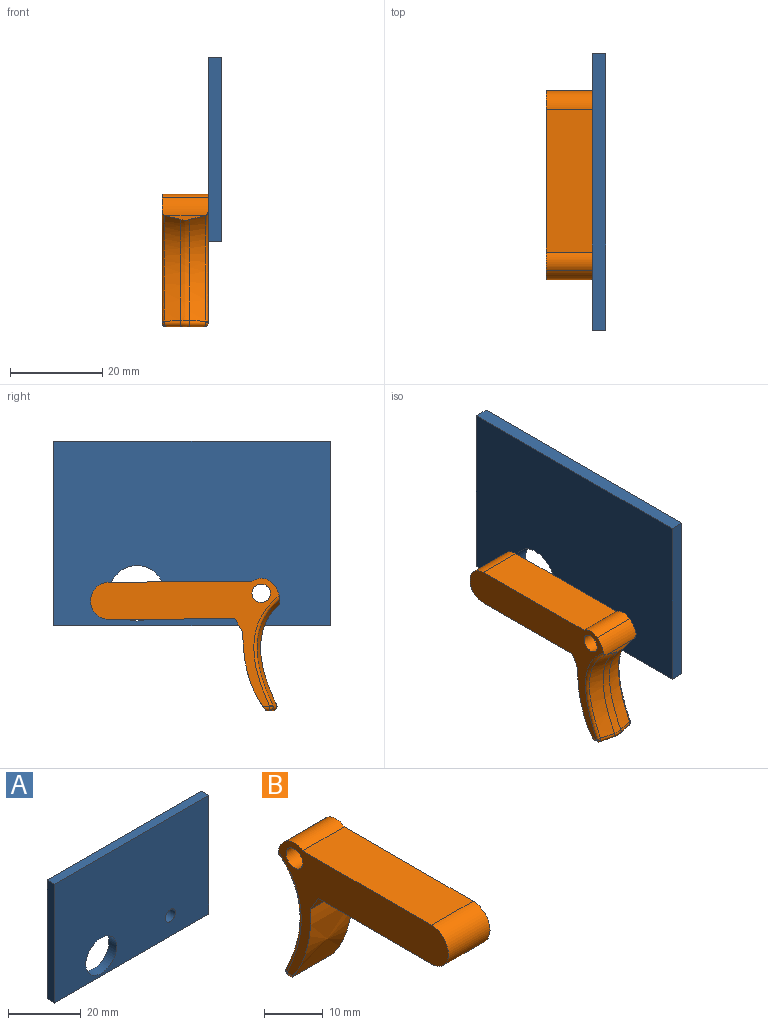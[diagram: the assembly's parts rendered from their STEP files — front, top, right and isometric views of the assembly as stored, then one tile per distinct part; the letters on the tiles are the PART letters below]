
ASSEMBLY  parts=2 mates=1
PART A: 8 faces, bbox 60x3x40 mm
  f0: plane 60x3mm, normal (0,0,-1), area 180mm2, adj f1,f5,f6,f7
  f1: plane 40x3mm, normal (1,0,0), area 120mm2, adj f0,f2,f6,f7
  f2: plane 60x3mm, normal (0,0,1), area 180mm2, adj f1,f5,f6,f7
  f3: cylinder r=2mm len=4mm, axis (0,1,0), area 37.7mm2, adj f6,f7
  f4: cylinder r=6mm len=12mm, axis (0,1,0), area 113.1mm2, adj f6,f7
  f5: plane 40x3mm, normal (-1,0,0), area 120mm2, adj f0,f2,f6,f7
  f6: plane 60x40mm, normal (0,-1,0), area 2274.3mm2, adj f0,f1,f2,f3,f4,f5
  f7: plane 60x40mm, normal (0,1,0), area 2274.3mm2, adj f0,f1,f2,f3,f4,f5
PART B: 27 faces, bbox 10.4x43.6x30.6 mm
  f0: cylinder r=4.04mm len=10mm, axis (-1,0,0), area 127mm2, adj f1,f7,f9,f10
  f1: plane 27.18x10mm, normal (0,0,-1), area 271.8mm2, adj f0,f2,f9,f10
  f2: plane 10x3.03mm, normal (0,-0.87,-0.5), area 35mm2, adj f1,f3,f9,f10
  f3: extruded ~16.65x10mm, area 176.3mm2, adj f2,f9,f10,f22,f24,f25
  f4: plane 8.2x0.99mm, normal (0,0,-1), area 5.1mm2, adj f16,f18,f21,f22,f24,f25
  f5: plane 8.11x1.11mm, normal (0,1,0), area 4.1mm2, adj f11,f12,f15,f26
  f6: cylinder r=3.25mm len=10mm, axis (-1,0,0), area 43.1mm2, adj f7,f9,f10,f26
  f7: plane 30.93x10mm, normal (0,0,1), area 309.3mm2, adj f0,f6,f9,f10
  f8: cylinder r=2mm len=10mm, axis (-1,0,0), area 125.7mm2, adj f9,f10
  f9: plane 40.89x28.4mm, normal (1,0,0), area 343.7mm2, adj f0,f1,f2,f3,f6,f7,f8,f14
  f10: plane 40.89x28.4mm, normal (-1,0,0), area 343.7mm2, adj f0,f1,f2,f3,f6,f7,f8,f13
  f11: bspline ~26.91x6.81mm, area 86mm2, adj f5,f13,f15,f16,f26
  f12: bspline ~26.91x6.81mm, area 86mm2, adj f5,f14,f15,f21,f26
  f13: bspline ~27.3x8.05mm, area 24.6mm2, adj f10,f11,f17,f26
  f14: bspline ~27.35x8.1mm, area 24.6mm2, adj f9,f12,f20,f26
  f15: bspline ~22.99x4.94mm, area 46.8mm2, adj f5,f11,f12,f18
  f16: bspline ~5.21x2.48mm, area 6.3mm2, adj f4,f11,f17,f18,f19
  f17: bspline ~0.72x0.6mm, area 0.3mm2, adj f10,f13,f16,f19
  f18: bspline ~3.91x1.81mm, area 3.5mm2, adj f4,f15,f16,f21
  f19: bspline ~1.15x0.9mm, area 0.6mm2, adj f16,f17,f22
  f20: bspline ~0.73x0.65mm, area 0.3mm2, adj f9,f14,f21,f23
  f21: bspline ~5.22x2.49mm, area 6.3mm2, adj f4,f12,f18,f20,f23
  f22: cylinder r=0.9mm len=1.45mm, axis (0,1,0), area 1.2mm2, adj f3,f4,f10,f19,f24
  f23: bspline ~0.96x0.9mm, area 0.6mm2, adj f20,f21,f25
  f24: cylinder r=0.9mm len=9.63mm, axis (-1,0,0), area 7.4mm2, adj f3,f4,f22,f25
  f25: cylinder r=0.9mm len=1.45mm, axis (0,-1,0), area 1.2mm2, adj f3,f4,f9,f23,f24
  f26: cylinder r=5mm len=10mm, axis (-1,0,0), area 45.7mm2, adj f5,f6,f9,f10,f11,f12,f13,f14
PLACE A rot(axis=(0,0,-1),90deg) t=(-8,9.22,-2.62)mm fixed
PLACE B rot(axis=(0,0,-1),180deg) t=(-16,20.21,1.9)mm
MATE revolute B.f6 <-> A.f3  axis (1,0,0) through (-11,24.22,4.38)mm
